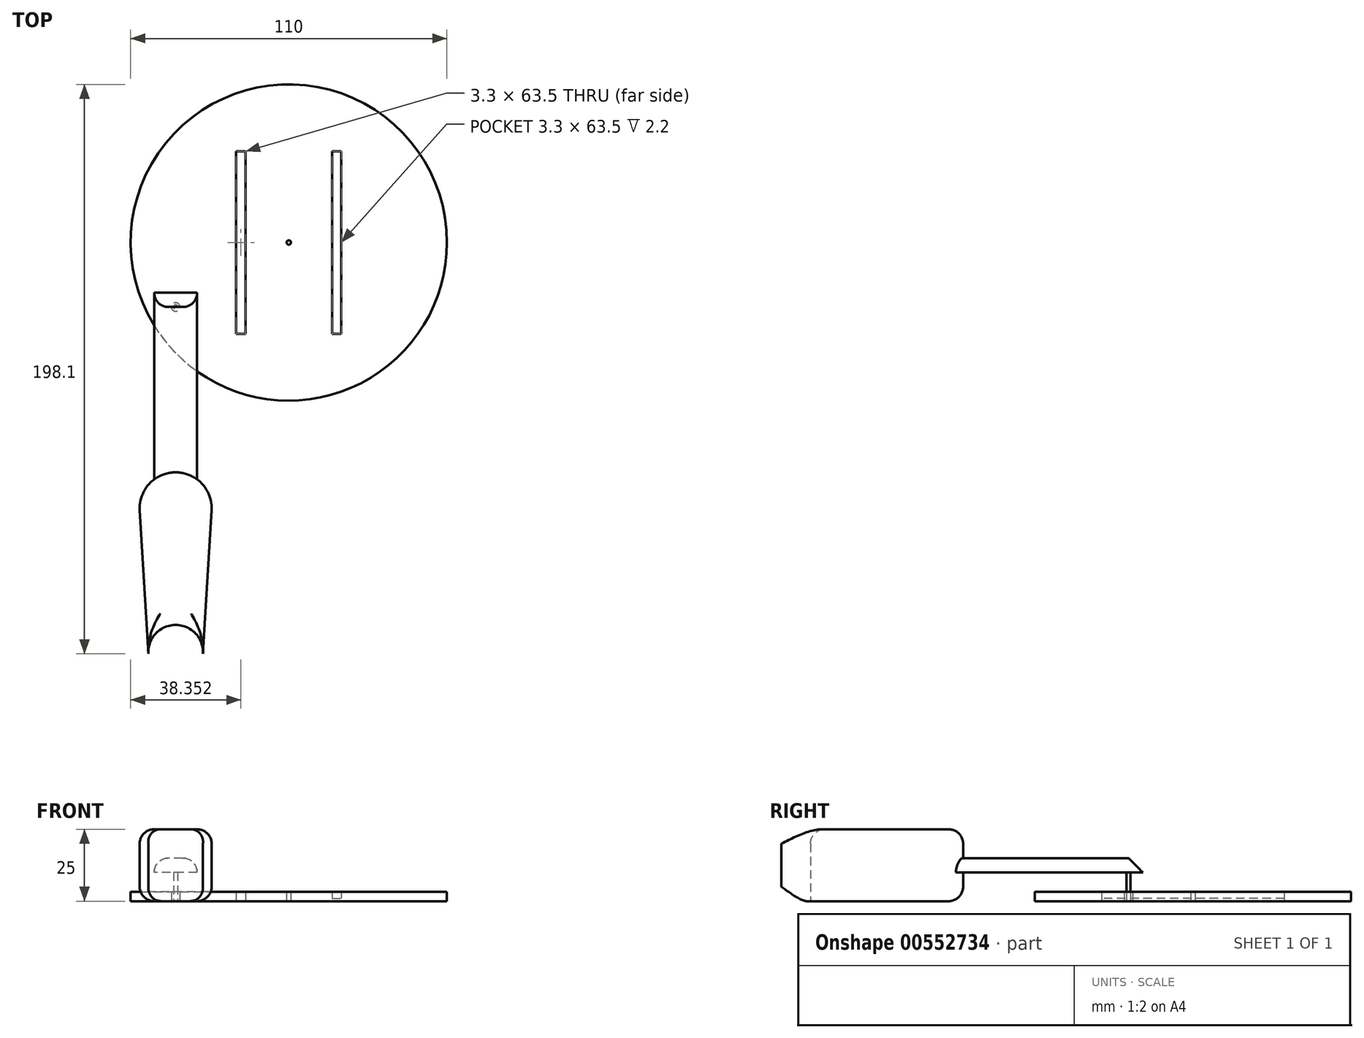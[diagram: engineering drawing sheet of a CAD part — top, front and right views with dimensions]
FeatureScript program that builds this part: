
annotation { "Feature Type Name" : "Feature", "Feature Type Description" : "" }
export const myFeature = defineFeature(function(context is Context, id is Id, definition is map)
    precondition{}
    {
        {
            var Q0;
            Q0=qCreatedBy(makeId("Top.planeOp"),FACE);
            var sketch = newSketch(context, id + "F0", { "sketchPlane" : qUnion([Q0])});
            skCircle(sketch, "E0", {"center": v(0, 25) * mm, "radius": 12.5 * mm});
            skLineSegment(sketch, "E1", {"start": v(-12.48, 24.26) * mm, "end": v(-9.5, -25.66) * mm});
            skLineSegment(sketch, "E2", {"start": v(12.48, 24.26) * mm, "end": v(9.5, -25.66) * mm});
            skArc(sketch, "E3", {"start": v(-9.5, -25.66) * mm, "mid": v(0, -15.57) * mm, "end": v(9.5, -25.66) * mm});
            skSolve(sketch);
        }
        {
            var Q0;
            {var subQ0=sQuery(id+"F0.wireOp",EDGE,"E0");var subQ1=makeQuery(id+"F0.imprint","INTERSECT",VERTEX,{"derivedFrom":[subQ0,sQuery(id+"F0.wireOp",EDGE,"E1")]});Q0=makeQuery(id+"F0.imprint","IMPRINT",FACE,{"disambiguationData":[TD([[makeQuery(id+"F0.imprint","IMPRINT",EDGE,{"disambiguationData":[TD([[subQ1,-1.0]])],"derivedFrom":subQ0}),1.0]])]});}
            var Q1;
            {var subQ0=sQuery(id+"F0.wireOp",EDGE,"E1");Q1=makeQuery(id+"F0.imprint","IMPRINT",FACE,{"disambiguationData":[TD([[makeQuery(id+"F0.imprint","IMPRINT",EDGE,{"derivedFrom":subQ0}),1.0]])]});}
            extrude(context, id + "F1", {"entities" : qUnion([Q0, Q1]), "depth" : 25 * mm});
        }
        {
            var Q0;
            Q0=makeQuery(id+"F1.opExtrude","CAP_EDGE",EDGE,{"disambiguationData":[OSD([sQuery(id+"F0.wireOp",EDGE,"E3")])],"isStart":false});
            var Q1;
            Q1=makeQuery(id+"F1.opExtrude","CAP_EDGE",EDGE,{"disambiguationData":[OSD([sQuery(id+"F0.wireOp",EDGE,"E1")])],"isStart":false});
            var Q2;
            Q2=makeQuery(id+"F1.opExtrude","CAP_EDGE",EDGE,{"disambiguationData":[OSD([sQuery(id+"F0.wireOp",EDGE,"E2")])],"isStart":false});
            fillet(context, id + "F2", {"entities" : qUnion([Q0, Q1, Q2]), "radius" : 5 * mm, "tangentPropagation" : true, "allowEdgeOverflow" : false});
        }
        {
            var Q0;
            Q0=makeQuery(id+"F1.opExtrude","CAP_EDGE",EDGE,{"disambiguationData":[OSD([sQuery(id+"F0.wireOp",EDGE,"E1")])],"isStart":true});
            fillet(context, id + "F3", {"entities" : qUnion([Q0]), "radius" : 5 * mm, "tangentPropagation" : true, "allowEdgeOverflow" : false});
        }
        {
            var Q0;
            Q0=qCreatedBy(makeId("Front.planeOp"),FACE);
            var sketch = newSketch(context, id + "F4", { "sketchPlane" : qUnion([Q0])});
            skLineSegment(sketch, "E4.bottom", {"start": v(7.48, 15) * mm, "end": v(-7.48, 15) * mm});
            skLineSegment(sketch, "E4.top", {"start": v(7.48, 10) * mm, "end": v(-7.48, 10) * mm});
            skLineSegment(sketch, "E4.left", {"start": v(7.48, 15) * mm, "end": v(7.48, 10) * mm});
            skLineSegment(sketch, "E4.right", {"start": v(-7.48, 15) * mm, "end": v(-7.48, 10) * mm});
            skSolve(sketch);
        }
        {
            var Q0;
            Q0=qSketchRegion(id+"F4",true);
            extrude(context, id + "F5", {"entities" : qUnion([Q0]), "operationType" : NewBodyOperationType.ADD, "oppositeDirection" : true, "depth" : 100 * mm});
        }
        {
            var Q0;
            Q0=makeQuery(id+"F5.opExtrude","SWEPT_EDGE",EDGE,{"disambiguationData":[OSD([sQuery(id+"F4.wireOp",EDGE,"E4.bottom"),sQuery(id+"F4.wireOp",EDGE,"E4.right")])]});
            var Q1;
            Q1=makeQuery(id+"F5.opExtrude","SWEPT_EDGE",EDGE,{"disambiguationData":[OSD([sQuery(id+"F4.wireOp",EDGE,"E4.bottom"),sQuery(id+"F4.wireOp",EDGE,"E4.left")])]});
            fillet(context, id + "F6", {"entities" : qUnion([Q0, Q1]), "radius" : 5 * mm, "tangentPropagation" : true, "allowEdgeOverflow" : false});
        }
        {
            var Q0;
            {var subQ0=sQuery(id+"F4.wireOp",EDGE,"E4.right");var subQ1=sQuery(id+"F4.wireOp",EDGE,"E4.bottom");Q0=makeQuery(id+"F6.opFillet","BLEND_EDGE",EDGE,{"blendedFrom":[makeQuery(id+"F5.opExtrude","SWEPT_EDGE",EDGE,{"disambiguationData":[OSD([subQ1,subQ0])]}),makeQuery(id+"F5.opExtrude","CAP_FACE",FACE,{"disambiguationData":[OSD([subQ1,sQuery(id+"F4.wireOp",EDGE,"E4.top"),sQuery(id+"F4.wireOp",EDGE,"E4.left"),subQ0])],"isStart":false})],"blendedInto":[makeQuery(id+"F5.opExtrude","CAP_FACE",FACE,{"disambiguationData":[OSD([subQ1,sQuery(id+"F4.wireOp",EDGE,"E4.top"),sQuery(id+"F4.wireOp",EDGE,"E4.left"),subQ0])],"isStart":false})]});}
            var Q1;
            {var subQ0=sQuery(id+"F4.wireOp",EDGE,"E4.left");var subQ1=sQuery(id+"F4.wireOp",EDGE,"E4.bottom");Q1=makeQuery(id+"F6.opFillet","BLEND_EDGE",EDGE,{"blendedFrom":[makeQuery(id+"F5.opExtrude","SWEPT_EDGE",EDGE,{"disambiguationData":[OSD([subQ1,subQ0])]}),makeQuery(id+"F5.opExtrude","CAP_FACE",FACE,{"disambiguationData":[OSD([subQ1,sQuery(id+"F4.wireOp",EDGE,"E4.top"),subQ0,sQuery(id+"F4.wireOp",EDGE,"E4.right")])],"isStart":false})],"blendedInto":[makeQuery(id+"F5.opExtrude","CAP_FACE",FACE,{"disambiguationData":[OSD([subQ1,sQuery(id+"F4.wireOp",EDGE,"E4.top"),subQ0,sQuery(id+"F4.wireOp",EDGE,"E4.right")])],"isStart":false})]});}
            chamfer(context, id + "F7", {"entities" : qUnion([Q0, Q1]), "width" : 5 * mm, "tangentPropagation" : true});
        }
        {
            var Q0;
            Q0=qCreatedBy(makeId("Top.planeOp"),FACE);
            var sketch = newSketch(context, id + "F8", { "sketchPlane" : qUnion([Q0])});
            skCircle(sketch, "E5", {"center": v(0, 95) * mm, "radius": 0.75 * mm});
            skSolve(sketch);
        }
        {
            var Q0;
            Q0=qSketchRegion(id+"F8",true);
            extrude(context, id + "F9", {"entities" : qUnion([Q0]), "operationType" : NewBodyOperationType.ADD, "depth" : 13.6 * mm});
        }
        {
            var Q0;
            Q0=qCreatedBy(makeId("Top.planeOp"),FACE);
            var sketch = newSketch(context, id + "F10", { "sketchPlane" : qUnion([Q0])});
            skCircle(sketch, "E6", {"center": v(39.35, 117.44) * mm, "radius": 55 * mm});
            skCircle(sketch, "E7", {"center": v(0, 95.01) * mm, "radius": 1.5 * mm});
            skCircle(sketch, "E8", {"center": v(39.35, 117.44) * mm, "radius": 0.75 * mm});
            skLineSegment(sketch, "E9.bottom", {"start": v(21.05, 149.19) * mm, "end": v(24.35, 149.19) * mm});
            skLineSegment(sketch, "E9.top", {"start": v(21.05, 85.69) * mm, "end": v(24.35, 85.69) * mm});
            skLineSegment(sketch, "E9.left", {"start": v(21.05, 149.19) * mm, "end": v(21.05, 85.69) * mm});
            skLineSegment(sketch, "E9.right", {"start": v(24.35, 149.19) * mm, "end": v(24.35, 85.69) * mm});
            skLineSegment(sketch, "E10.bottom", {"start": v(54.35, 149.19) * mm, "end": v(57.65, 149.19) * mm});
            skLineSegment(sketch, "E10.top", {"start": v(54.35, 85.69) * mm, "end": v(57.65, 85.69) * mm});
            skLineSegment(sketch, "E10.left", {"start": v(54.35, 149.19) * mm, "end": v(54.35, 85.69) * mm});
            skLineSegment(sketch, "E10.right", {"start": v(57.65, 149.19) * mm, "end": v(57.65, 85.69) * mm});
            skSolve(sketch);
        }
        {
            var Q0;
            Q0=makeQuery(id+"F10.imprint","IMPRINT",FACE,{"disambiguationData":[TD([[makeQuery(id+"F10.imprint","IMPRINT",EDGE,{"derivedFrom":sQuery(id+"F10.wireOp",EDGE,"E6")}),1.0]])]});
            extrude(context, id + "F11", {"entities" : qUnion([Q0]), "depth" : 3.2 * mm});
        }
        {
            var Q0;
            Q0=makeQuery(id+"F10.imprint","IMPRINT",FACE,{"disambiguationData":[TD([[makeQuery(id+"F10.imprint","IMPRINT",EDGE,{"derivedFrom":sQuery(id+"F10.wireOp",EDGE,"E9.bottom")}),-1.0]])]});
            var Q1;
            Q1=makeQuery(id+"F10.imprint","IMPRINT",FACE,{"disambiguationData":[TD([[makeQuery(id+"F10.imprint","IMPRINT",EDGE,{"derivedFrom":sQuery(id+"F10.wireOp",EDGE,"E10.bottom")}),-1.0]])]});
            extrude(context, id + "F12", {"entities" : qUnion([Q0, Q1]), "operationType" : NewBodyOperationType.ADD, "depth" : 1 * mm});
        }
    });
